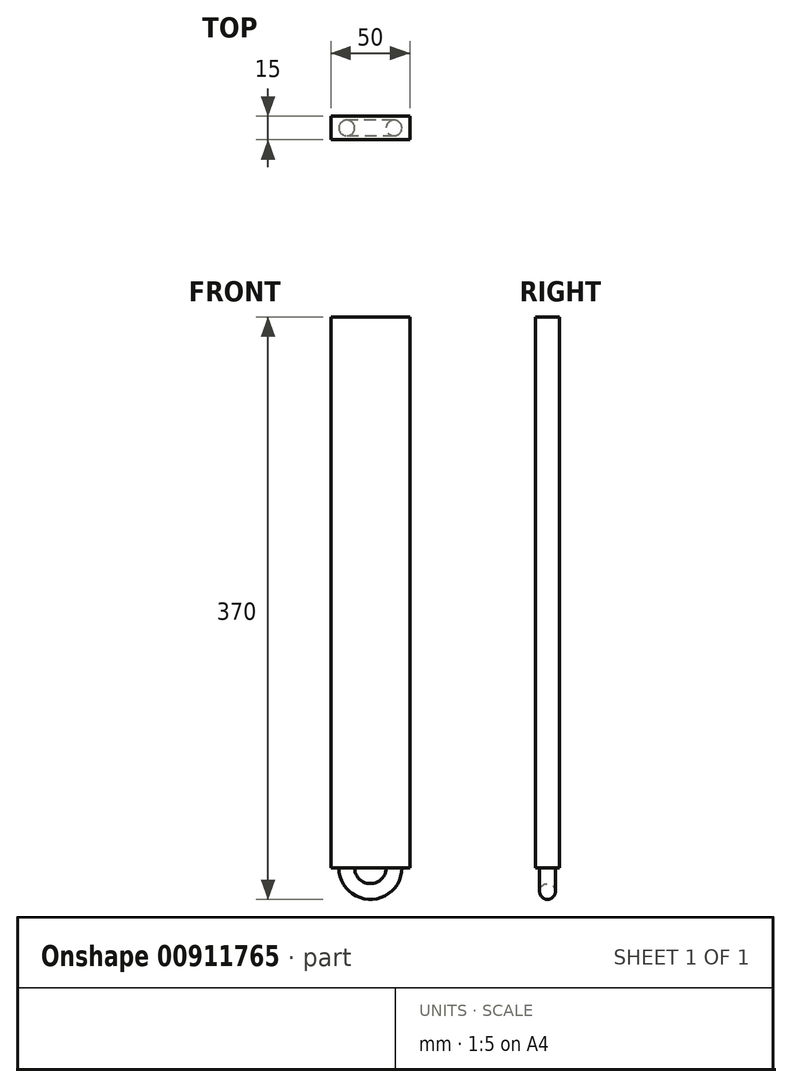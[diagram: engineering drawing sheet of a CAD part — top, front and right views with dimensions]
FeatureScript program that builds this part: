
annotation { "Feature Type Name" : "Feature", "Feature Type Description" : "" }
export const myFeature = defineFeature(function(context is Context, id is Id, definition is map)
    precondition{}
    {
        {
            var Q0;
            Q0=qCreatedBy(makeId("Top.planeOp"),FACE);
            var sketch = newSketch(context, id + "F0", { "sketchPlane" : qUnion([Q0])});
            skLineSegment(sketch, "E0.bottom", {"start": v(-25, 7.5) * mm, "end": v(25, 7.5) * mm});
            skLineSegment(sketch, "E0.top", {"start": v(-25, -7.5) * mm, "end": v(25, -7.5) * mm});
            skLineSegment(sketch, "E0.left", {"start": v(-25, 7.5) * mm, "end": v(-25, -7.5) * mm});
            skLineSegment(sketch, "E0.right", {"start": v(25, 7.5) * mm, "end": v(25, -7.5) * mm});
            skSolve(sketch);
        }
        {
            var Q0;
            Q0=qSketchRegion(id+"F0",true);
            extrude(context, id + "F1", {"entities" : qUnion([Q0]), "depth" : 350 * mm, "offsetDistance" : 25 * mm});
        }
        {
            var Q0;
            Q0=makeQuery(id+"F1.opExtrude","CAP_FACE",FACE,{"disambiguationData":[OSD([sQuery(id+"F0.wireOp",EDGE,"E0.bottom"),sQuery(id+"F0.wireOp",EDGE,"E0.top"),sQuery(id+"F0.wireOp",EDGE,"E0.left"),sQuery(id+"F0.wireOp",EDGE,"E0.right")])],"isStart":true});
            var sketch = newSketch(context, id + "F2", { "sketchPlane" : qUnion([Q0])});
            skPoint(sketch, "E1", {"position": v(-15, 0) * mm});
            skPoint(sketch, "E2", {"position": v(15, 0) * mm});
            skCircle(sketch, "E3", {"center": v(15, 0) * mm, "radius": 5 * mm});
            skCircle(sketch, "E4", {"center": v(-15, 0) * mm, "radius": 5 * mm});
            skLineSegment(sketch, "E5", {"start": v(0, -10.6) * mm, "end": v(0, 12.8) * mm});
            skPoint(sketch, "E5.endSnap0", {"position": v(0, 7.5) * mm});
            skSolve(sketch);
        }
        {
            var Q0;
            Q0=qSketchRegion(id+"F2",true);
            var Q1;
            Q1=sQuery(id+"F2.wireOp",EDGE,"E5");
            revolve(context, id + "F3", {"operationType" : NewBodyOperationType.ADD, "surfaceOperationType" : NewSurfaceOperationType.NEW, "entities" : qUnion([Q0]), "axis" : qUnion([Q1]), "revolveType" : RevolveType.FULL});
        }
    });
